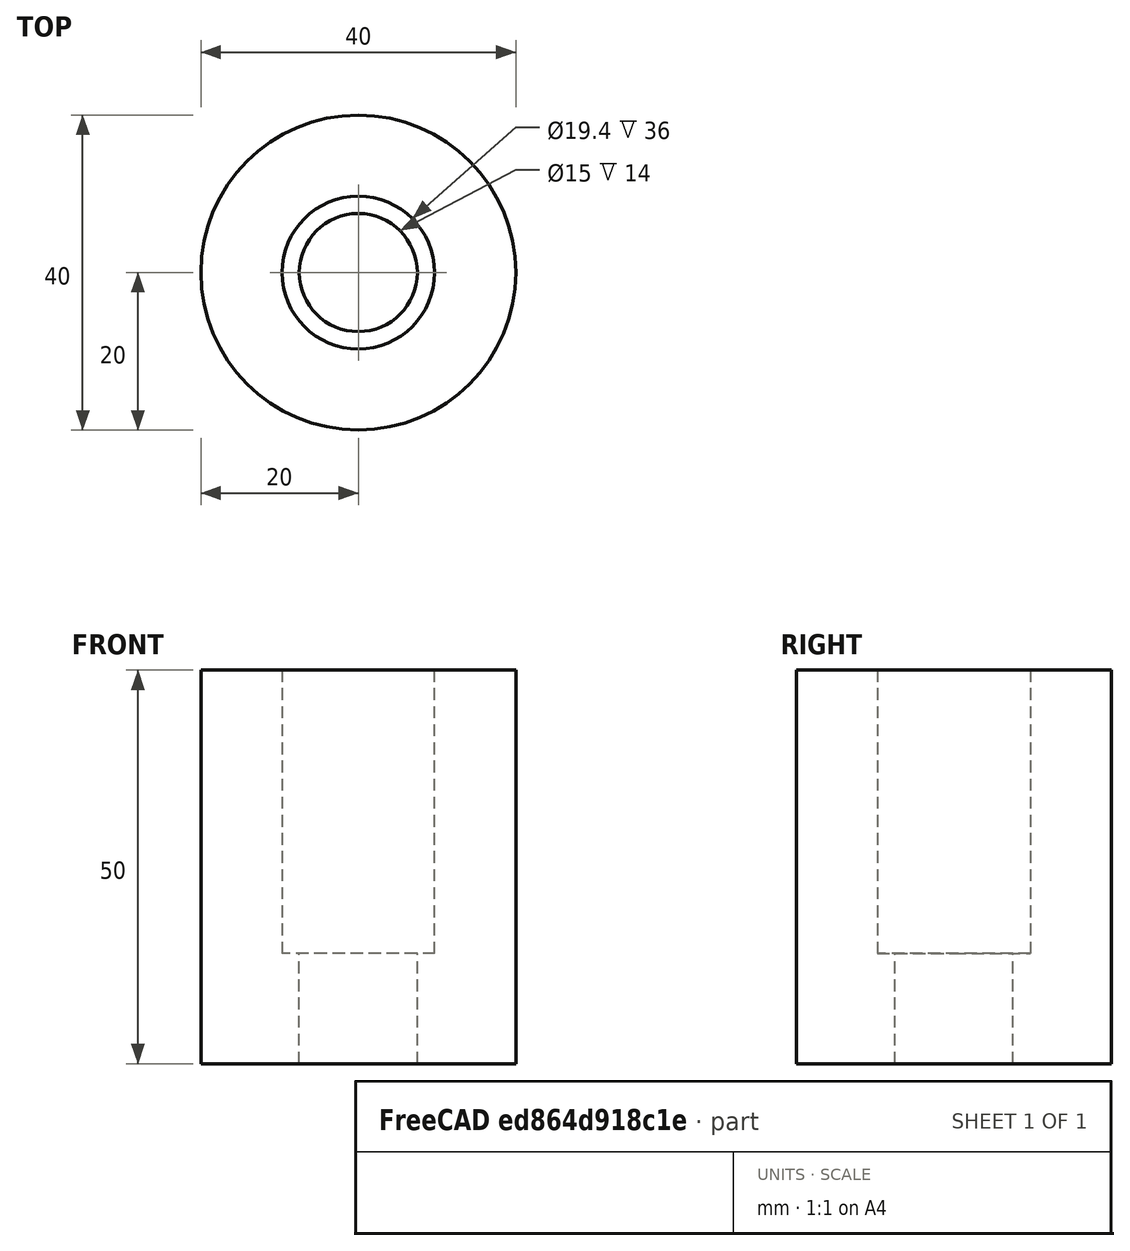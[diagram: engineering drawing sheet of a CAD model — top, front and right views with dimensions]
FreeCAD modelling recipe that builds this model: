
FCSTD DOCUMENT  (FreeCAD 0.21R33771 (Git))
Label: SFT-Mk5-Flywheel Mount
License: Public Domain
LicenseURL: https://en.wikipedia.org/wiki/Public_domain
objects: PartDesign::CoordinateSystem×1, Part::FeaturePython×1, Part::Cylinder×1, Part::Cut×1, App::Part×1
note: 4 computed .brp shape members not serialized (recipe doc carries the construction recipe); baked Part::Feature solids carry a one-line shape summary decoded from their .brp

FEATURE [PartDesign::CoordinateSystem] LCS_Origin
  AttacherType = Attacher::AttachEngine3D
  MapMode = 2
  Support = -> [X_Axis]
FEATURE [Part::FeaturePython] Tube  label="Base"  # WARN: FeaturePython — macro-defined, semantics opaque (R4)
  AttacherType = Attacher::AttachEngine3D
  Height = 50
  InnerRadius = 7.5
  OuterRadius = 20
FEATURE [Part::Cylinder] Cylinder  label="Bearing Hole cutter"
  Angle = 360
  AttacherType = Attacher::AttachEngine3D
  FirstAngle = 0
  Height = 50
  Placement = pos=(0,0,14) rot=(0,0,1;0rad)
  Radius = 9.7
  SecondAngle = 0
FEATURE [Part::Cut] Cut
  Base = -> Tube
  Tool = -> Cylinder
FEATURE [App::Part] Flywheel_Mount  label="Flywheel Mount"
  Group = -> [LCS_Origin,Tube,Cylinder,Cut]
  Origin = -> Origin
